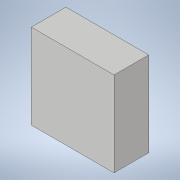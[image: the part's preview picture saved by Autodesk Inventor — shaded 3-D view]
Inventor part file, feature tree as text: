
AUTODESK INVENTOR PART (.ipt)
format: ipt  version: 2021 (Build 250183000, 183)  size: 107,520 bytes
history: native  units: mm
features: extrude x4, sketch x4
ambient origin geometry x8: Origin, YZ Plane, XZ Plane, XY Plane, X Axis, Y Axis, Z Axis, Center Point
bodies: Body1 (feature_tree)
feature tree (8):
  extrude  "Extrusion2"  Depth=139.0mm
  extrude  "Extrusion3"  Depth=20.0mm TaperAngle=0.0deg
  extrude  "Extrusion4"  Depth=10.0mm TaperAngle=0.0deg
  extrude  "Extrusion5"  [1 undecoded]
  sketch  "Sketch2"  dims[d4=135.0mm d5=139.0mm]
  sketch  "Sketch3"  dims[d6=75.0mm d7=0.0mm d8=20.0mm d9=0.0mm]
  sketch  "Sketch4"  dims[d10=20.0mm d11=0.0mm d12=10.0mm d13=0.0mm]
  sketch  "Sketch5"
note: 1 required parameter value undecoded (feature->parameter linkage not recoverable at this tier; creation-order binding heuristic only, values carry confidence <= 0.55)
